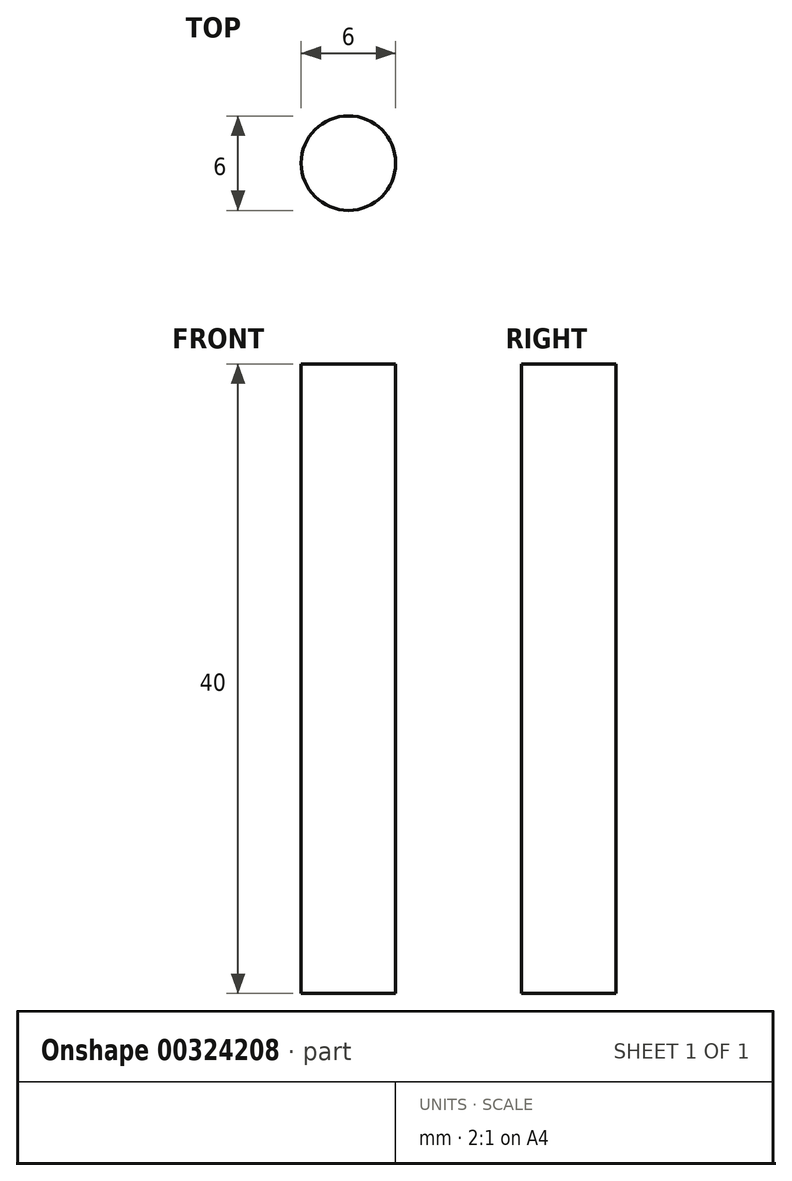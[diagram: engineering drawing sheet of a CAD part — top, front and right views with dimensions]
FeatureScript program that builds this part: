
annotation { "Feature Type Name" : "Feature", "Feature Type Description" : "" }
export const myFeature = defineFeature(function(context is Context, id is Id, definition is map)
    precondition{}
    {
        {
            var Q0;
            Q0=qCreatedBy(makeId("Top.planeOp"),FACE);
            var sketch = newSketch(context, id + "F0", { "sketchPlane" : qUnion([Q0])});
            skCircle(sketch, "E0", {"center": v(0, 0) * mm, "radius": 3 * mm});
            skSolve(sketch);
        }
        {
            var Q0;
            Q0=makeQuery(id+"F0.imprint","IMPRINT",FACE,{"disambiguationData":[TD([[makeQuery(id+"F0.imprint","IMPRINT",EDGE,{"derivedFrom":sQuery(id+"F0.wireOp",EDGE,"E0")}),1.0]])]});
            extrude(context, id + "F1", {"entities" : qUnion([Q0]), "depth" : 40 * mm});
        }
    });
